# Revit family: RSC - pannello residenza
name_source: partatom
category: Curtain Panels
revit_build: Autodesk Revit 2014 (Build: 20130308_1515(x64)
units: mm (PartAtom-declared; Revit-internal decimal feet)

## types (6) — shared parameters
Analytic Construction = <None>

## per-type parameters (varying)
| type | c_bamboo | rsc - pannello 620x1070 | rsc - pannello 620x750 |
| Pannello 900mm x 1200mm | <By Category> | Yes | Yes |
| Pannello 900mm x 800mm | Bamboo | Yes | Yes |
| rsc - pannello tipo760 | Bamboo | No | No |
| rsc - pannello tipo1780 | Bamboo | Yes | Yes |
| rsc - pannello tipo 620x1070 | Bamboo | Yes | Yes |
| rsc - pannello tpo 620x750 | Bamboo | No | Yes |

type visibility flags (boolean, named after types; folded from table):
- Pannello 900mm x 1200mm: Yes: Pannello 900mm x 1200mm, Pannello 900mm x 800mm, rsc - pannello tipo1780, rsc - pannello tipo760
- Pannello 900mm x 800mm: Yes: Pannello 900mm x 800mm, rsc - pannello tipo1780, rsc - pannello tipo760
- rsc - pannello tipo760: Yes: rsc - pannello tipo760
- rsc - pannello tipo1780: Yes: rsc - pannello tipo1780, rsc - pannello tipo760
- rsc - pannello tipo 620x1070: Yes: (none)
- rsc - pannello tpo 620x750: Yes: (none)

## geometry (parser evidence)
native form markers: Sweep x13
no freeform markers — native parametric forms only
